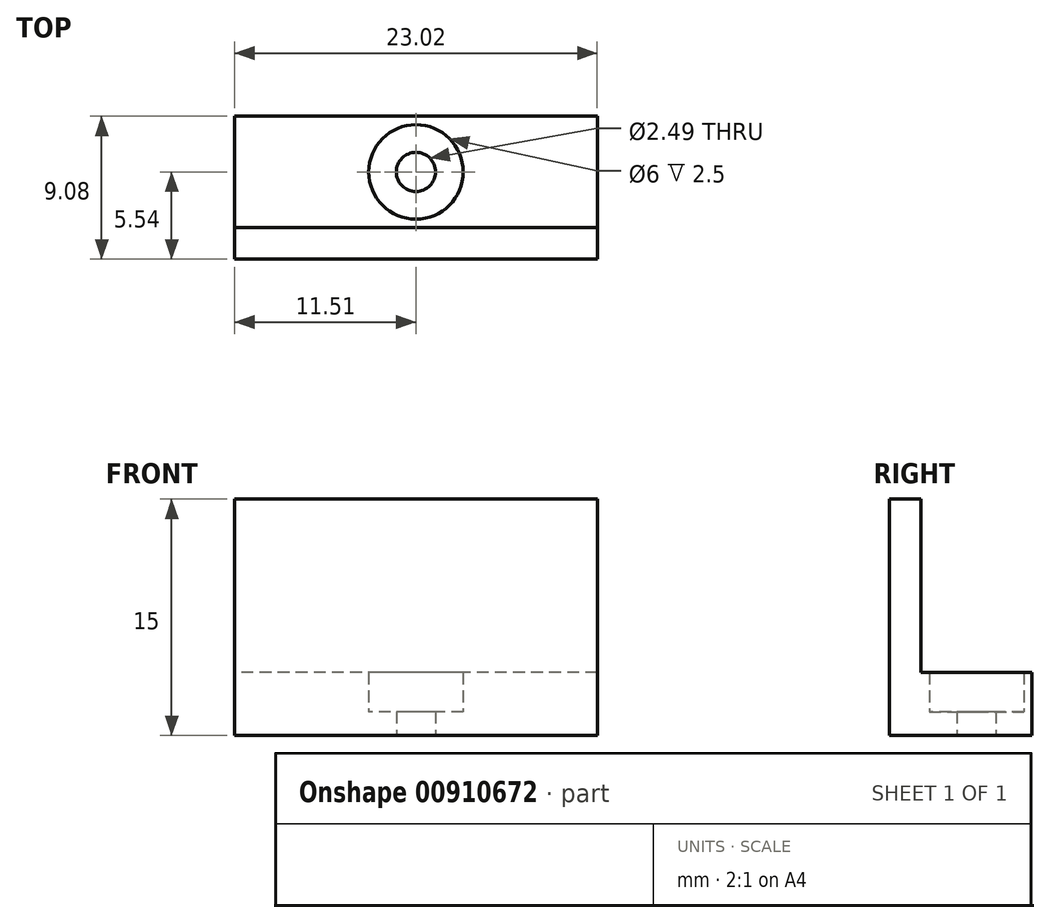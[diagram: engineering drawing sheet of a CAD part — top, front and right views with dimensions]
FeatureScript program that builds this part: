
annotation { "Feature Type Name" : "Feature", "Feature Type Description" : "" }
export const myFeature = defineFeature(function(context is Context, id is Id, definition is map)
    precondition{}
    {
        {
            var Q0;
            Q0=qCreatedBy(makeId("Top.planeOp"),FACE);
            var sketch = newSketch(context, id + "F0", { "sketchPlane" : qUnion([Q0])});
            skCircle(sketch, "E0", {"center": v(0, 0) * mm, "radius": 1.25 * mm});
            skCircle(sketch, "E1", {"center": v(0, 0) * mm, "radius": 3 * mm});
            skCircle(sketch, "E2", {"center": v(0, 0) * mm, "radius": 3.54 * mm});
            skLineSegment(sketch, "E3.bottom", {"start": v(13.51, 3.54) * mm, "end": v(-13.51, 3.54) * mm});
            skLineSegment(sketch, "E3.top", {"start": v(13.51, -3.53) * mm, "end": v(-13.51, -3.53) * mm});
            skLineSegment(sketch, "E3.left", {"start": v(13.51, 3.54) * mm, "end": v(13.51, -3.53) * mm});
            skLineSegment(sketch, "E3.right", {"start": v(-13.51, 3.54) * mm, "end": v(-13.51, -3.53) * mm});
            skLineSegment(sketch, "E4.bottom", {"start": v(-13.51, -3.53) * mm, "end": v(-11.51, -3.53) * mm});
            skLineSegment(sketch, "E4.top", {"start": v(-13.52, 3.54) * mm, "end": v(-11.52, 3.54) * mm});
            skLineSegment(sketch, "E4.left", {"start": v(-13.51, -3.53) * mm, "end": v(-13.51, 3.54) * mm});
            skLineSegment(sketch, "E4.right", {"start": v(-11.51, -3.53) * mm, "end": v(-11.52, 3.54) * mm});
            skLineSegment(sketch, "E5.bottom", {"start": v(13.51, -3.53) * mm, "end": v(11.51, -3.53) * mm});
            skLineSegment(sketch, "E5.top", {"start": v(13.51, 3.54) * mm, "end": v(11.51, 3.54) * mm});
            skLineSegment(sketch, "E5.left", {"start": v(13.51, -3.53) * mm, "end": v(13.51, 3.54) * mm});
            skLineSegment(sketch, "E5.right", {"start": v(11.51, -3.53) * mm, "end": v(11.51, 3.54) * mm});
            skSolve(sketch);
        }
        {
            var Q0;
            Q0=makeQuery(id+"F0.imprint","IMPRINT",FACE,{"disambiguationData":[TD([[makeQuery(id+"F0.imprint","IMPRINT",EDGE,{"derivedFrom":sQuery(id+"F0.wireOp",EDGE,"E0")}),-1.0]])]});
            extrude(context, id + "F1", {"entities" : qUnion([Q0]), "depth" : 1.5 * mm, "offsetDistance" : 25 * mm});
        }
        {
            var Q0;
            Q0=makeQuery(id+"F0.imprint","IMPRINT",FACE,{"disambiguationData":[TD([[makeQuery(id+"F0.imprint","IMPRINT",EDGE,{"derivedFrom":sQuery(id+"F0.wireOp",EDGE,"E1")}),-1.0]])]});
            var Q1;
            {var subQ5=sQuery(id+"F0.wireOp",EDGE,"E4.right");Q1=makeQuery(id+"F0.imprint","IMPRINT",FACE,{"disambiguationData":[TD([[makeQuery(id+"F0.imprint","IMPRINT",EDGE,{"derivedFrom":subQ5}),-1.0]])]});}
            var Q2;
            {var subQ5=sQuery(id+"F0.wireOp",EDGE,"E5.right");Q2=makeQuery(id+"F0.imprint","IMPRINT",FACE,{"disambiguationData":[TD([[makeQuery(id+"F0.imprint","IMPRINT",EDGE,{"derivedFrom":subQ5}),1.0]])]});}
            extrude(context, id + "F2", {"entities" : qUnion([Q0, Q1, Q2]), "operationType" : NewBodyOperationType.ADD, "depth" : 4 * mm, "offsetDistance" : 25 * mm});
        }
        {
            var Q0;
            Q0=makeQuery(id+"F2.opExtrude","SWEPT_FACE",FACE,{"disambiguationData":[OSD([sQuery(id+"F0.wireOp",EDGE,"E3.top")])]});
            var sketch = newSketch(context, id + "F3", { "sketchPlane" : qUnion([Q0])});
            skLineSegment(sketch, "E6.bottom", {"start": v(-11.51, 0) * mm, "end": v(11.51, 0) * mm});
            skLineSegment(sketch, "E6.top", {"start": v(-11.52, 15) * mm, "end": v(11.51, 15) * mm});
            skLineSegment(sketch, "E6.left", {"start": v(-11.51, 0) * mm, "end": v(-11.51, 15) * mm});
            skLineSegment(sketch, "E6.right", {"start": v(11.51, 0) * mm, "end": v(11.51, 15) * mm});
            skSolve(sketch);
        }
        {
            var Q0;
            {var subQ0=sQuery(id+"F3.wireOp",EDGE,"E6.top");Q0=makeQuery(id+"F3.imprint","IMPRINT",FACE,{"disambiguationData":[TD([[makeQuery(id+"F3.imprint","IMPRINT",EDGE,{"derivedFrom":subQ0}),-1.0]])]});}
            var Q1;
            {var subQ0=sQuery(id+"F3.wireOp",EDGE,"E6.bottom");Q1=makeQuery(id+"F3.imprint","IMPRINT",FACE,{"disambiguationData":[TD([[makeQuery(id+"F3.imprint","IMPRINT",EDGE,{"derivedFrom":subQ0}),-1.0]])]});}
            extrude(context, id + "F4", {"entities" : qUnion([Q0, Q1]), "operationType" : NewBodyOperationType.ADD, "depth" : 2 * mm, "offsetDistance" : 25 * mm});
        }
    });
